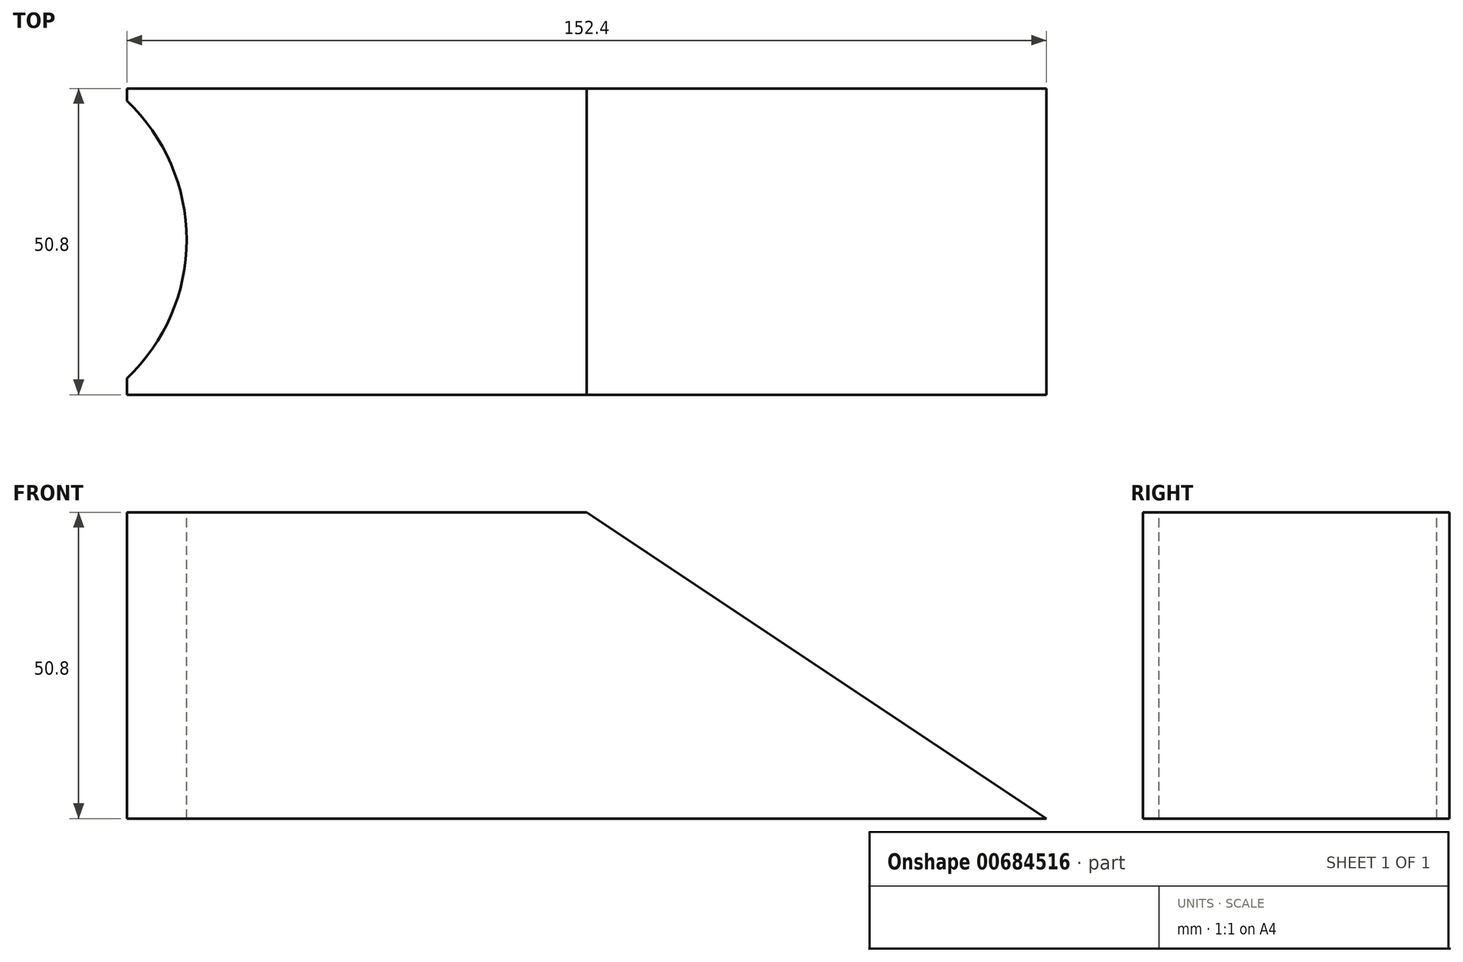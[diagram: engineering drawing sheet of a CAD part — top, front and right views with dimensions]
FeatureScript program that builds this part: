
annotation { "Feature Type Name" : "Feature", "Feature Type Description" : "" }
export const myFeature = defineFeature(function(context is Context, id is Id, definition is map)
    precondition{}
    {
        {
            var Q0;
            Q0=qCreatedBy(makeId("Front.planeOp"),FACE);
            var sketch = newSketch(context, id + "F0", { "sketchPlane" : qUnion([Q0])});
            skLineSegment(sketch, "E0", {"start": v(-92.23, 0) * mm, "end": v(-92.23, -50.8) * mm});
            skLineSegment(sketch, "E1", {"start": v(-92.23, 0) * mm, "end": v(-16.03, 0) * mm});
            skLineSegment(sketch, "E2", {"start": v(-92.23, -50.8) * mm, "end": v(60.17, -50.8) * mm});
            skLineSegment(sketch, "E3", {"start": v(60.17, -50.8) * mm, "end": v(-16.03, 0) * mm});
            skSolve(sketch);
        }
        {
            var Q0;
            Q0 = qSketchRegion(id + "F0", true);
            extrude(context, id + "F1", {"entities" : qUnion([Q0]), "oppositeDirection" : true, "depth" : 50.8 * mm, "offsetDistance" : 25.4 * mm});
        }
        {
            var Q0;
            Q0=makeQuery(id+"F1.opExtrude","SWEPT_FACE",FACE,{"disambiguationData":[OSD([sQuery(id+"F0.wireOp",EDGE,"E1")])]});
            var sketch = newSketch(context, id + "F2", { "sketchPlane" : qUnion([Q0])});
            skArc(sketch, "E4", {"start": v(-92.23, 0) * mm, "mid": v(-80.36, 26.24) * mm, "end": v(-93.06, 52.1) * mm});
            skSolve(sketch);
        }
        {
            var Q0;
            Q0=sQuery(id+"F2.wireOp",VERTEX,"E4.center");
            var Q1;
            Q1=makeQuery(id+"F1.opExtrude","SWEPT_BODY",BODY,{"disambiguationData":[OSD([sQuery(id+"F0.wireOp",EDGE,"E0"),sQuery(id+"F0.wireOp",EDGE,"E1"),sQuery(id+"F0.wireOp",EDGE,"E2"),sQuery(id+"F0.wireOp",EDGE,"E3")])]});
            hole(context, id + "F3", {"style" : HoleStyle.SIMPLE, "endStyle" : HoleEndStyle.THROUGH, "holeDiameter" : 63.5 * mm, "majorDiameter" : 6.35 * mm, "isTappedThrough" : true, "tappedDepth" : 12.7 * mm, "tapClearance" : 3, "locations" : qUnion([Q0]), "scope" : qUnion([Q1])});
        }
    });
